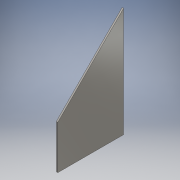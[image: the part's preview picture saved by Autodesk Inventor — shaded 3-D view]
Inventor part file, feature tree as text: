
AUTODESK INVENTOR PART (.ipt)
format: ipt  version: 2016 (Build 200138000, 138)  size: 109,568 bytes
history: native  units: mm
features: extrude x1, sketch x1
ambient origin geometry x8: Origin, YZ Plane, XZ Plane, XY Plane, X Axis, Y Axis, Z Axis, Center Point
bodies: Solid1 (feature_tree)
feature tree (2):
  extrude  "Extrusion1"  Depth=1760.0mm
  sketch  "Sketch1"  dims[d0=2656.64mm d1=1760.0mm d2=45.0deg d3=60.0mm d4=0.0mm]
